# Revit family: Badminton-System_Competition_BM10
name_source: partatom
category: Generic Models
revit_build: Autodesk Revit 2018 (Build: 20180423_1000(x64)
units: mm (PartAtom-declared; Revit-internal decimal feet)

## family parameters
Always vertical = Yes
Can host rebar = No
Cut with Voids When Loaded = No
OmniClass Number = 23.40.50.34.14
OmniClass Title = Gymnasium Equipment
Part Type = Normal
Room Calculation Point = No
Round Connector Dimension = Use Diameter
Shared = No
Work Plane-Based = No

## types (1)
- Badminton-System_Competition_BM10
    Building Codes = https://www.brpbybison.com
    Construction Details = https://www.arcat.com
    Description = IPI by Bison Gymnasium Equipment
    Green Building-LEED = https://www.arcat.com
    Height = 5' - 1"
    Installation-Fabrication = http://www.ipibybison.com
    Keynote = 11 66 00
    Length = 20' - 0"
    Manufacturer = BRP by bison
    Manufacturer Fax = 888-438-5312
    Manufacturer Website = http://www.ipibybison.com
    Model = As Specified
    Net Frame Material = Fabric - Black - Netting Frame
    Net Height = 2' - 6"
    Netting = Finish - IPI by Bison - White Netting
    Post Diameter = 0' - 1 21/32"
    Post Finish = Powder Coat - White
    Product Data = http://www.arcat.com
    Revision = R1_2018-09
    Sales Information = http://www.ipibybison.com
    Specification = https://www.arcat.com
    Test Data = http://www.ipibybison.com
    URL = https://ipibybison.com

## geometry (parser evidence)
native form markers: Blend x4, Sweep x2
no freeform markers — native parametric forms only
